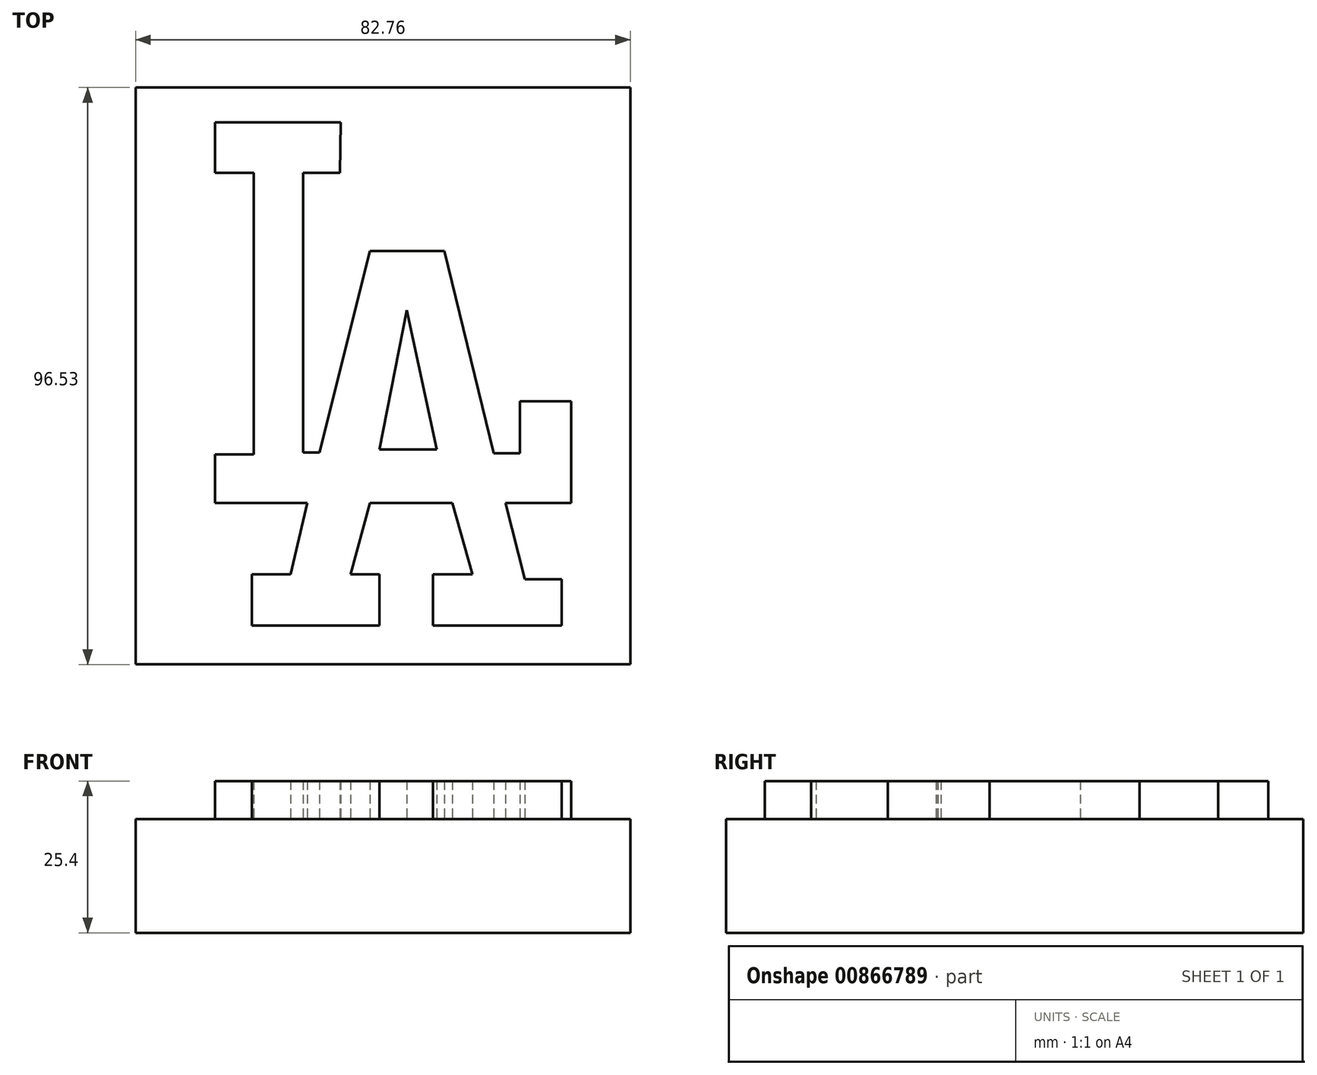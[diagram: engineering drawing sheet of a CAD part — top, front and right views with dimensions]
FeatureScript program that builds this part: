
annotation { "Feature Type Name" : "Feature", "Feature Type Description" : "" }
export const myFeature = defineFeature(function(context is Context, id is Id, definition is map)
    precondition{}
    {
        {
            var Q0;
            Q0=qCreatedBy(makeId("Top.planeOp"),FACE);
            var sketch = newSketch(context, id + "F0", { "sketchPlane" : qUnion([Q0])});
            skLineSegment(sketch, "E0", {"start": v(-13.52, 42.2) * mm, "end": v(-34.58, 42.2) * mm});
            skLineSegment(sketch, "E1", {"start": v(-34.58, 42.2) * mm, "end": v(-34.58, 33.77) * mm});
            skLineSegment(sketch, "E2", {"start": v(-34.58, 33.77) * mm, "end": v(-28.1, 33.77) * mm});
            skLineSegment(sketch, "E3", {"start": v(-28.1, 33.77) * mm, "end": v(-28.1, -13.36) * mm});
            skLineSegment(sketch, "E4", {"start": v(-28.1, -13.36) * mm, "end": v(-34.58, -13.36) * mm});
            skLineSegment(sketch, "E5", {"start": v(-34.58, -13.36) * mm, "end": v(-34.58, -21.46) * mm});
            skLineSegment(sketch, "E6", {"start": v(-34.58, -21.46) * mm, "end": v(-19.12, -21.46) * mm});
            skLineSegment(sketch, "E7", {"start": v(-19.12, -21.46) * mm, "end": v(-21.95, -33.45) * mm});
            skLineSegment(sketch, "E8", {"start": v(-21.95, -33.45) * mm, "end": v(-28.42, -33.45) * mm});
            skLineSegment(sketch, "E9", {"start": v(-28.42, -33.45) * mm, "end": v(-28.42, -42.03) * mm});
            skLineSegment(sketch, "E10", {"start": v(-28.42, -42.03) * mm, "end": v(-7.05, -42.03) * mm});
            skLineSegment(sketch, "E11", {"start": v(-7.05, -42.03) * mm, "end": v(-7.05, -33.45) * mm});
            skLineSegment(sketch, "E12", {"start": v(-7.05, -33.45) * mm, "end": v(-11.9, -33.45) * mm});
            skLineSegment(sketch, "E13", {"start": v(-11.9, -33.45) * mm, "end": v(-8.67, -21.46) * mm});
            skLineSegment(sketch, "E14", {"start": v(-8.67, -21.46) * mm, "end": v(5.1, -21.46) * mm});
            skLineSegment(sketch, "E15", {"start": v(5.1, -21.46) * mm, "end": v(8.48, -33.45) * mm});
            skLineSegment(sketch, "E16", {"start": v(8.48, -33.45) * mm, "end": v(1.86, -33.45) * mm});
            skLineSegment(sketch, "E17", {"start": v(1.86, -33.45) * mm, "end": v(1.86, -42.03) * mm});
            skLineSegment(sketch, "E18", {"start": v(1.86, -42.03) * mm, "end": v(23.4, -42.03) * mm});
            skLineSegment(sketch, "E19", {"start": v(23.4, -42.03) * mm, "end": v(23.4, -34.26) * mm});
            skLineSegment(sketch, "E20", {"start": v(23.4, -34.26) * mm, "end": v(17.25, -34.26) * mm});
            skLineSegment(sketch, "E21", {"start": v(17.25, -34.26) * mm, "end": v(14, -21.46) * mm});
            skLineSegment(sketch, "E22", {"start": v(14, -21.46) * mm, "end": v(25.02, -21.46) * mm});
            skLineSegment(sketch, "E23", {"start": v(25.02, -21.46) * mm, "end": v(25.02, -4.45) * mm});
            skLineSegment(sketch, "E24", {"start": v(25.02, -4.45) * mm, "end": v(16.44, -4.45) * mm});
            skLineSegment(sketch, "E25", {"start": v(16.44, -4.45) * mm, "end": v(16.44, -13.2) * mm});
            skLineSegment(sketch, "E26", {"start": v(16.44, -13.2) * mm, "end": v(12.07, -13.2) * mm});
            skLineSegment(sketch, "E27", {"start": v(12.07, -13.2) * mm, "end": v(3.8, 20.65) * mm});
            skLineSegment(sketch, "E28", {"start": v(3.8, 20.65) * mm, "end": v(-8.67, 20.65) * mm});
            skLineSegment(sketch, "E29", {"start": v(-8.67, 20.65) * mm, "end": v(-17.09, -13.04) * mm});
            skLineSegment(sketch, "E30", {"start": v(-17.09, -13.04) * mm, "end": v(-19.84, -13.04) * mm});
            skLineSegment(sketch, "E31", {"start": v(-19.84, -13.04) * mm, "end": v(-19.84, 33.77) * mm});
            skLineSegment(sketch, "E32", {"start": v(-19.84, 33.77) * mm, "end": v(-13.69, 33.77) * mm});
            skLineSegment(sketch, "E33", {"start": v(-13.69, 33.77) * mm, "end": v(-13.52, 42.2) * mm});
            skLineSegment(sketch, "E34", {"start": v(-2.51, 10.77) * mm, "end": v(-7.05, -12.55) * mm});
            skLineSegment(sketch, "E35", {"start": v(-7.05, -12.55) * mm, "end": v(2.51, -12.55) * mm});
            skLineSegment(sketch, "E36", {"start": v(2.51, -12.55) * mm, "end": v(-2.51, 10.77) * mm});
            skLineSegment(sketch, "E37.bottom", {"start": v(-46.89, 46.4) * mm, "end": v(46.24, 46.4) * mm});
            skLineSegment(sketch, "E37.top", {"start": v(-46.89, -46.73) * mm, "end": v(46.24, -46.73) * mm});
            skLineSegment(sketch, "E37.left", {"start": v(-46.89, 46.4) * mm, "end": v(-46.89, -46.73) * mm});
            skLineSegment(sketch, "E37.right", {"start": v(46.24, 46.4) * mm, "end": v(46.24, -46.73) * mm});
            skSolve(sketch);
        }
        {
            var Q0;
            Q0=makeQuery(id+"F0.imprint","IMPRINT",FACE,{"disambiguationData":[TD([[makeQuery(id+"F0.imprint","IMPRINT",EDGE,{"derivedFrom":sQuery(id+"F0.wireOp",EDGE,"E0")}),1.0]])]});
            extrude(context, id + "F1", {"entities" : qUnion([Q0]), "depth" : 25.4 * mm, "offsetDistance" : 25.4 * mm});
        }
        {
            var Q0;
            Q0=qCreatedBy(makeId("Top.planeOp"),FACE);
            var sketch = newSketch(context, id + "F2", { "sketchPlane" : qUnion([Q0])});
            skLineSegment(sketch, "E38.bottom", {"start": v(-47.86, 48.02) * mm, "end": v(34.9, 48.02) * mm});
            skLineSegment(sketch, "E38.top", {"start": v(-47.86, -48.5) * mm, "end": v(34.9, -48.5) * mm});
            skLineSegment(sketch, "E38.left", {"start": v(-47.86, 48.02) * mm, "end": v(-47.86, -48.5) * mm});
            skLineSegment(sketch, "E38.right", {"start": v(34.9, 48.02) * mm, "end": v(34.9, -48.5) * mm});
            skSolve(sketch);
        }
        {
            var Q0;
            Q0=makeQuery(id+"F2.imprint","IMPRINT",FACE,{"disambiguationData":[TD([[makeQuery(id+"F2.imprint","IMPRINT",EDGE,{"derivedFrom":sQuery(id+"F2.wireOp",EDGE,"E38.bottom")}),-1.0]])]});
            extrude(context, id + "F3", {"entities" : qUnion([Q0]), "operationType" : NewBodyOperationType.ADD, "depth" : 19.05 * mm, "offsetDistance" : 25.4 * mm});
        }
    });
